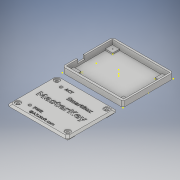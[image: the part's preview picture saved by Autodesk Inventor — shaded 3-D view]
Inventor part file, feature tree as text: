
AUTODESK INVENTOR PART (.ipt)
format: ipt  version: 2019 (Build 230136000, 136)  size: 3,121,664 bytes
history: native  units: mm
features: sketch x44, extrude x28, move_body x21, direct_edit x10, delete_face x3, chamfer x2, split x1
ambient origin geometry x8: Origin, YZ Plane, XZ Plane, XY Plane, X Axis, Y Axis, Z Axis, Center Point
bodies: Solid1 (feature_tree), Solid2 (feature_tree), Solid3 (feature_tree)
feature tree (109):
  sketch  "Sketch1"  dims[d16=3.0mm d17=3.0mm]
  sketch  "Sketch2"  dims[d18=3.0mm d19=3.0mm]
  extrude  "Extrusion1"  Depth=3.0mm
  extrude  "Extrusion2"  Depth=3.0mm
  extrude  "Extrusion3"  Depth=8.0mm
  direct_edit  "Direct Edit1"
  sketch  "Sketch5"  dims[d24=8.0mm d25=8.0mm]
  extrude  "Extrusion4"  Depth=8.0mm
  direct_edit  "Direct Edit2"
  extrude  "Extrusion5"  Depth=8.0mm
  split  "Split1"
  move_body  "Move Body1"
  sketch  "Sketch9"  dims[d41=7.0mm d42=4.0mm]
  extrude  "Extrusion6"  Depth=8.0mm
  sketch  "Sketch11"  dims[d46=4.0mm d47=9.872mm]
  sketch  "Sketch12"  dims[d48=51.171798mm d49=14.0mm]
  extrude  "Extrusion7"  Depth=10.0mm TaperAngle=0.0deg
  direct_edit  "Direct Edit3"
  sketch  "Sketch14"  dims[d53=0.0mm d54=0.0mm d55=0.5mm d56=0.0mm d57=0.0mm d58=0.5mm]
  delete_face  "Delete Face1"
  delete_face  "Delete Face2"
  delete_face  "Delete Face3"
  extrude  "Extrusion8"  TaperAngle=0.0deg  [1 undecoded]
  sketch  "Sketch15"  dims[d59=0.0mm d60=0.0mm d61=1.0mm d62=0.0mm d63=0.0mm d64=1.0mm]
  extrude  "Extrusion9"  Depth=4.0mm
  sketch  "Sketch17"  dims[d69=3.0mm d70=3.0mm]
  extrude  "Extrusion10"  Depth=7.0mm
  sketch  "Sketch19"  dims[d74=9.75mm d75=-5.75mm d76=61.75mm d77=4.0mm d78=0.0mm]
  extrude  "Extrusion11"  Depth=9.872mm
  sketch  "Sketch21"  dims[d82=0.0mm d83=0.0mm d84=0.15mm d85=2.0mm d86=0.0mm]
  sketch  "Sketch22"  dims[d87=8.0mm d88=8.0mm]
  extrude  "Extrusion12"  Depth=14.0mm
  extrude  "Extrusion13"  Depth=2.0mm TaperAngle=0.0deg
  sketch  "Sketch24"  dims[d91=8.0mm d92=8.0mm]
  sketch  "Sketch25"  dims[d93=8.0mm d94=8.0mm]
  sketch  "Sketch26"  dims[d95=2.5mm d96=0.0mm d97=2.0mm d98=0.0mm d99=2.0mm d100=0.0mm]
  extrude  "Extrusion14"  Depth=0.5mm TaperAngle=0.0deg
  extrude  "Extrusion15"  Depth=1.0mm TaperAngle=0.0deg
  extrude  "Extrusion16"  Depth=3.0mm
  extrude  "Extrusion17"  Depth=3.0mm
  sketch  "Sketch31"  dims[d116=3.0mm]
  sketch  "Sketch32"  dims[d117=3.0mm]
  sketch  "Sketch33"  dims[d118=3.0mm]
  extrude  "Extrusion18"  Depth=4.0mm TaperAngle=0.0deg
  direct_edit  "Direct Edit4"
  move_body  "Move Body2"
  extrude  "Extrusion19"  Depth=4.0mm TaperAngle=0.0deg
  extrude  "Extrusion20"  Depth=4.0mm TaperAngle=0.0deg
  direct_edit  "Direct Edit5"
  direct_edit  "Direct Edit6"
  extrude  "Extrusion21"  Depth=2.0mm TaperAngle=0.0deg
  extrude  "Extrusion22"  Depth=8.0mm
  sketch  "Sketch38"  dims[d128=0.0mm d129=0.0mm d130=-0.5mm]
  extrude  "Extrusion23"  Depth=8.0mm
  extrude  "Extrusion24"  Depth=8.0mm
  direct_edit  "Direct Edit7"
  direct_edit  "Direct Edit8"
  direct_edit  "Direct Edit9"
  sketch  "Sketch41"  dims[d137=-9.25mm d138=0.0mm d139=0.75mm]
  sketch  "Sketch42"  dims[d140=1.0mm d141=0.0mm]
  direct_edit  "Direct Edit10"
  extrude  "Extrusion25"  Depth=8.0mm
  extrude  "Extrusion26"  Depth=2.0mm TaperAngle=0.0deg
  chamfer  "Chamfer1"  Distance=2.0mm
  chamfer  "Chamfer2"  Distance=2.0mm
  extrude  "Extrusion27"  Depth=0.6mm TaperAngle=0.0deg
  extrude  "Extrusion28"  Depth=3.0mm
  sketch  "Sketch3"  dims[d20=8.0mm d21=8.0mm]
  sketch  "Sketch4"  dims[d22=8.0mm d23=8.0mm]
  sketch  "Sketch6"  dims[d26=8.0mm d27=8.0mm]
  sketch  "Sketch7"  dims[d28=1.5mm d29=0.0mm d30=10.0mm d31=0.0mm]
  sketch  "Sketch8"  dims[d32=2.0mm d33=0.0mm d34=0.0mm d35=0.0mm d36=-0.5mm]
  sketch  "Sketch10"  dims[d44=4.0mm d45=7.0mm]
  sketch  "Sketch13"  dims[d50=13.3mm d51=2.0mm d52=0.0mm]
  sketch  "Sketch16"  dims[d65=0.0mm d66=0.0mm d67=0.5mm d68=3.0mm]
  sketch  "Sketch18"  dims[d71=3.0mm d72=4.0mm d73=0.0mm]
  sketch  "Sketch20"  dims[d79=7.0mm d80=4.0mm d81=0.0mm]
  sketch  "Sketch23"  dims[d89=8.0mm d90=8.0mm]
  sketch  "Sketch27"  dims[d105=3.2mm]
  sketch  "Sketch28"  dims[d106=3.2mm d107=2.0mm d108=0.0mm]
  sketch  "Sketch29"  dims[d109=1.0mm d110=0.0mm d111=0.6mm d112=0.0mm]
  sketch  "Sketch30"  dims[d113=0.6mm d114=0.0mm d115=3.0mm]
  sketch  "Sketch34"  dims[d119=5.0mm d120=0.0mm]
  sketch  "Sketch35"  dims[d121=1.0mm d122=0.0mm]
  sketch  "Sketch36"  dims[d123=1.0mm d124=0.0mm]
  sketch  "Sketch37"  dims[d125=0.0mm d126=0.0mm d127=-0.5mm]
  sketch  "Sketch39"  dims[d131=0.0mm d132=0.0mm d133=-0.2mm]
  sketch  "Sketch40"  dims[d134=0.0mm d135=0.0mm d136=-0.2mm]
  sketch  "Sketch43"  dims[d142=0.8mm d143=0.0mm]
  sketch  "Sketch44"  dims[d144=0.0mm d145=0.0mm d146=1.0mm d147=0.0mm d148=0.0mm d149=0.4mm d150=1.0mm d151=0.0mm d152=1.0mm d153=0.0mm d154=6.0mm d155=6.0mm d156=6.0mm d157=6.0mm d158=1.0mm d159=0.0mm d160=1.0mm d161=0.0mm d162=0.0mm d163=0.0mm d164=1.0mm d165=0.0mm d166=0.0mm d167=-0.5mm d168=0.0mm d169=0.0mm d170=1.1mm d171=0.0mm d172=0.0mm d173=0.5mm d174=0.0mm d175=0.0mm d176=4.0mm d177=0.0mm d178=0.0mm d179=-0.25mm d180=1.0mm d181=1.0mm d182=1.0mm d183=1.0mm d184=3.0mm d185=0.0mm d186=2.0mm d187=0.0mm d188=2.0mm d189=2.0mm d190=45.0deg d191=2.0mm d192=2.0mm d193=45.0deg d194=0.6mm d195=0.0mm d196=0.6mm d197=0.0mm]
  move_body  "Move1"
  move_body  "Move2"
  move_body  "Move3"
  move_body  "Move4"
  move_body  "Move5"
  move_body  "Move6"
  move_body  "Move7"
  move_body  "Move8"
  move_body  "Move9"
  move_body  "Move10"
  move_body  "Move11"
  move_body  "Move12"
  move_body  "Move13"
  move_body  "Move14"
  move_body  "Move15"
  move_body  "Move16"
  move_body  "Move17"
  move_body  "Move18"
  move_body  "Move19"
note: 1 required parameter value undecoded (feature->parameter linkage not recoverable at this tier; creation-order binding heuristic only, values carry confidence <= 0.55)
